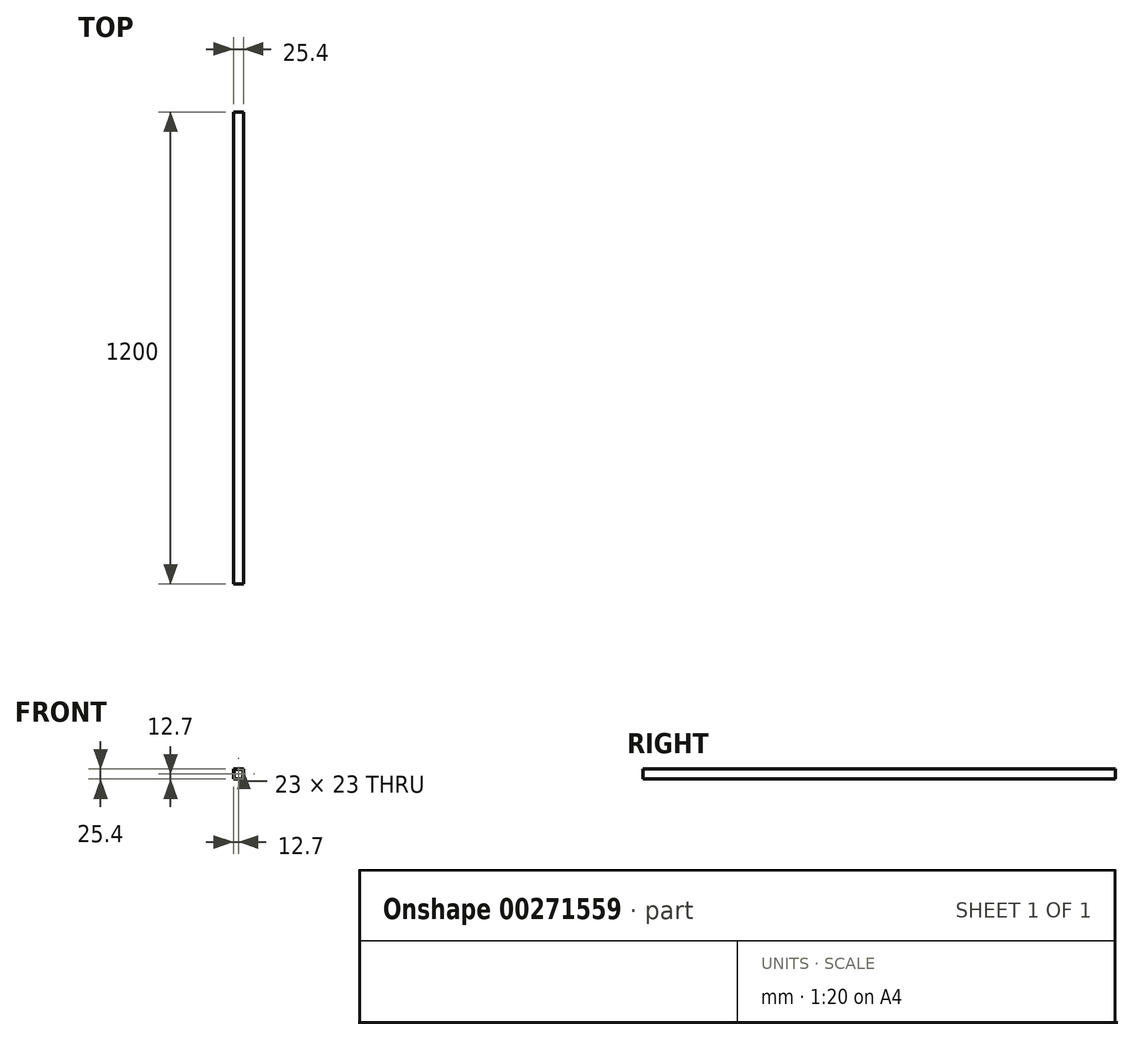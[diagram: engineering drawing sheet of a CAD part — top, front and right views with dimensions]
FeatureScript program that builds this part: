
annotation { "Feature Type Name" : "Feature", "Feature Type Description" : "" }
export const myFeature = defineFeature(function(context is Context, id is Id, definition is map)
    precondition{}
    {
        {
            var Q0;
            Q0=qCreatedBy(makeId("Top.planeOp"),FACE);
            var sketch = newSketch(context, id + "F0", { "sketchPlane" : qUnion([Q0])});
            skLineSegment(sketch, "E0.bottom", {"start": v(12.7, -600) * mm, "end": v(-12.7, -600) * mm});
            skLineSegment(sketch, "E0.top", {"start": v(12.7, 600) * mm, "end": v(-12.7, 600) * mm});
            skLineSegment(sketch, "E0.left", {"start": v(12.7, -600) * mm, "end": v(12.7, 600) * mm});
            skLineSegment(sketch, "E0.right", {"start": v(-12.7, -600) * mm, "end": v(-12.7, 600) * mm});
            skPoint(sketch, "E0.middle", {"position": v(0, 0) * mm});
            skSolve(sketch);
        }
        {
            var Q0;
            Q0 = qSketchRegion(id + "F0", true);
            extrude(context, id + "F1", {"entities" : qUnion([Q0]), "depth" : 25.4 * mm});
        }
        {
            var Q0;
            Q0=makeQuery(id+"F1.opExtrude","SWEPT_FACE",FACE,{"disambiguationData":[OSD([sQuery(id+"F0.wireOp",EDGE,"E0.bottom")])]});
            var Q1;
            Q1=makeQuery(id+"F1.opExtrude","SWEPT_FACE",FACE,{"disambiguationData":[OSD([sQuery(id+"F0.wireOp",EDGE,"E0.top")])]});
            shell(context, id + "F2", {"entities" : qUnion([Q0, Q1]), "thickness" : 1.2 * mm});
        }
    });
